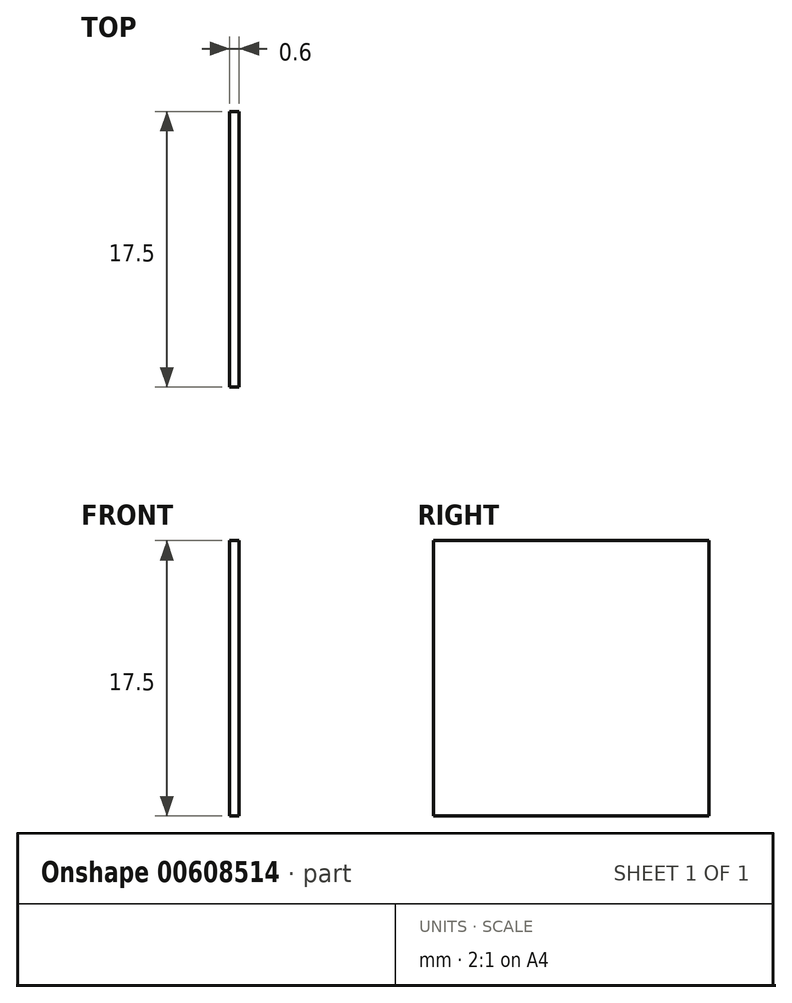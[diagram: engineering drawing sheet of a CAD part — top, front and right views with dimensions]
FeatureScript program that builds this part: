
annotation { "Feature Type Name" : "Feature", "Feature Type Description" : "" }
export const myFeature = defineFeature(function(context is Context, id is Id, definition is map)
    precondition{}
    {
        {
            var Q0;
            Q0=qCreatedBy(makeId("Right.planeOp"),FACE);
            var sketch = newSketch(context, id + "F0", { "sketchPlane" : qUnion([Q0])});
            skLineSegment(sketch, "E0.bottom", {"start": v(0, 0) * mm, "end": v(17.5, 0) * mm});
            skLineSegment(sketch, "E0.top", {"start": v(0, -17.5) * mm, "end": v(17.5, -17.5) * mm});
            skLineSegment(sketch, "E0.left", {"start": v(0, 0) * mm, "end": v(0, -17.5) * mm});
            skLineSegment(sketch, "E0.right", {"start": v(17.5, 0) * mm, "end": v(17.5, -17.5) * mm});
            skSolve(sketch);
        }
        {
            var Q0;
            Q0=makeQuery(id+"F0.imprint","IMPRINT",FACE,{"disambiguationData":[TD([[makeQuery(id+"F0.imprint","IMPRINT",EDGE,{"derivedFrom":sQuery(id+"F0.wireOp",EDGE,"E0.bottom")}),-1.0]])]});
            extrude(context, id + "F1", {"entities" : qUnion([Q0]), "depth" : .6 * mm, "offsetDistance" : 25 * mm});
        }
    });
